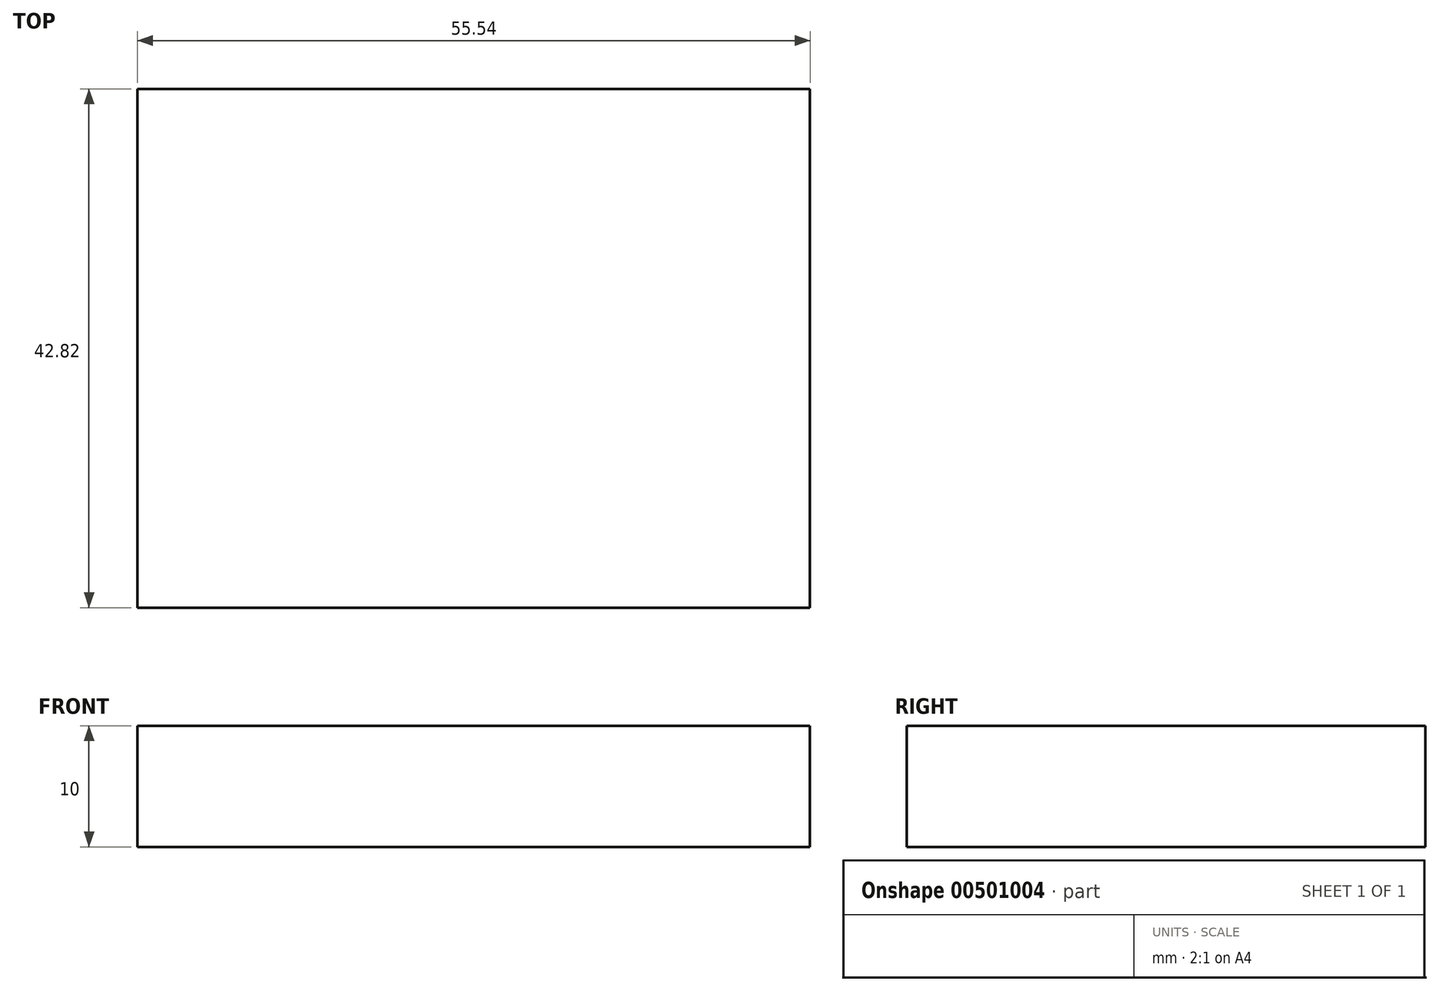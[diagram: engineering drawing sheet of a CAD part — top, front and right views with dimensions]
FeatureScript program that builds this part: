
annotation { "Feature Type Name" : "Feature", "Feature Type Description" : "" }
export const myFeature = defineFeature(function(context is Context, id is Id, definition is map)
    precondition{}
    {
        {
            var Q0;
            Q0=qCreatedBy(makeId("Top.planeOp"),FACE);
            var sketch = newSketch(context, id + "F0", { "sketchPlane" : qUnion([Q0])});
            skLineSegment(sketch, "E0.bottom", {"start": v(27.77, 21.41) * mm, "end": v(-27.77, 21.41) * mm});
            skLineSegment(sketch, "E0.top", {"start": v(27.77, -21.41) * mm, "end": v(-27.77, -21.41) * mm});
            skLineSegment(sketch, "E0.left", {"start": v(27.77, 21.41) * mm, "end": v(27.77, -21.41) * mm});
            skLineSegment(sketch, "E0.right", {"start": v(-27.77, 21.41) * mm, "end": v(-27.77, -21.41) * mm});
            skPoint(sketch, "E0.middle", {"position": v(0, 0) * mm});
            skSolve(sketch);
        }
        {
            var Q0;
            Q0=makeQuery(id+"F0.imprint","IMPRINT",FACE,{"disambiguationData":[TD([[makeQuery(id+"F0.imprint","IMPRINT",EDGE,{"derivedFrom":sQuery(id+"F0.wireOp",EDGE,"E0.bottom")}),1.0]])]});
            extrude(context, id + "F1", {"entities" : qUnion([Q0]), "depth" : 10 * mm, "offsetDistance" : 25 * mm});
        }
    });
